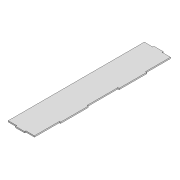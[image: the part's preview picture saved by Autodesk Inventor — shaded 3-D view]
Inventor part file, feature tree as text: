
AUTODESK INVENTOR PART (.ipt)
format: ipt  version: 2021 (Build 250183000, 183)  size: 124,928 bytes
history: native  units: mm
features: other x1, extrude x1, sketch x1
ambient origin geometry x8: Origin, YZ Plane, XZ Plane, XY Plane, X Axis, Y Axis, Z Axis, Center Point
bodies: Body1 (feature_tree)
feature tree (3):
  other  "Твердое тело1"
  extrude  "Выдавливание1"  Depth=4.0mm TaperAngle=0.0deg
  sketch  "Эскиз1"
